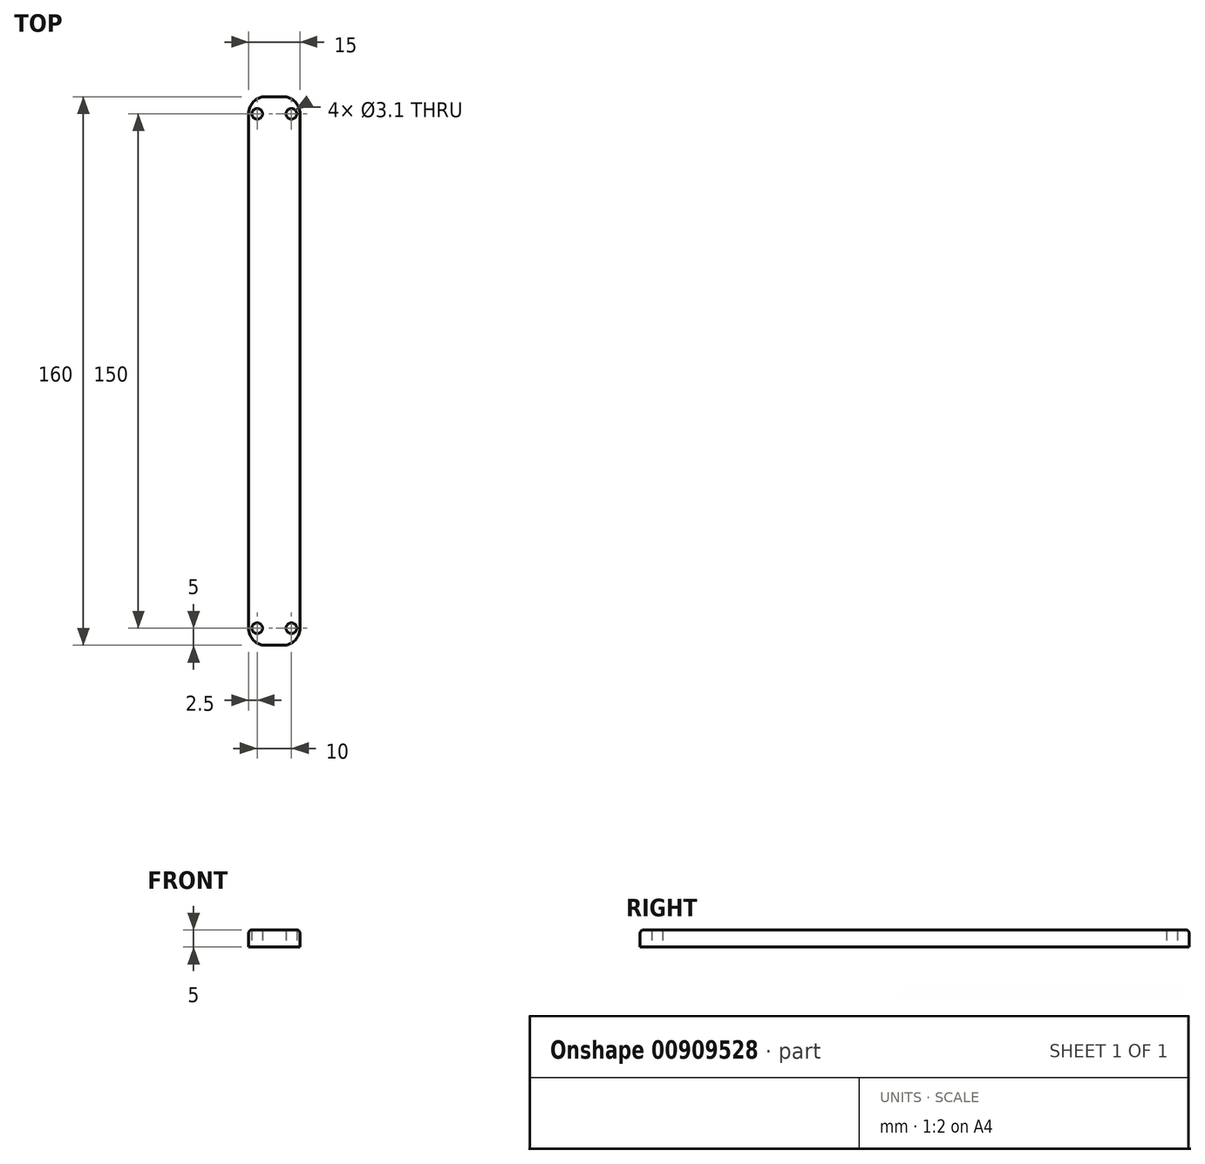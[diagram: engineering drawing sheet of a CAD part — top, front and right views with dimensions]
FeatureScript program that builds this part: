
annotation { "Feature Type Name" : "Feature", "Feature Type Description" : "" }
export const myFeature = defineFeature(function(context is Context, id is Id, definition is map)
    precondition{}
    {
        {
            var Q0;
            Q0=qCreatedBy(makeId("Top.planeOp"),FACE);
            var sketch = newSketch(context, id + "F0", { "sketchPlane" : qUnion([Q0])});
            skLineSegment(sketch, "E0.bottom", {"start": v(-7.5, -80) * mm, "end": v(7.5, -80) * mm});
            skLineSegment(sketch, "E0.top", {"start": v(-7.5, 80) * mm, "end": v(7.5, 80) * mm});
            skLineSegment(sketch, "E0.left", {"start": v(-7.5, -80) * mm, "end": v(-7.5, 80) * mm});
            skLineSegment(sketch, "E0.right", {"start": v(7.5, -80) * mm, "end": v(7.5, 80) * mm});
            skPoint(sketch, "E0.middle", {"position": v(0, 0) * mm});
            skLineSegment(sketch, "E1", {"start": v(0, 0) * mm, "end": v(0, 75) * mm});
            skLineSegment(sketch, "E2", {"start": v(0, 0) * mm, "end": v(0, -75) * mm});
            skLineSegment(sketch, "E3", {"start": v(0, -75) * mm, "end": v(-5, -75) * mm});
            skCircle(sketch, "E4", {"center": v(-5, -75) * mm, "radius": 1.55 * mm});
            skLineSegment(sketch, "E5", {"start": v(0, -75) * mm, "end": v(5, -75) * mm});
            skCircle(sketch, "E6", {"center": v(5, -75) * mm, "radius": 1.55 * mm});
            skLineSegment(sketch, "E7", {"start": v(0, 75) * mm, "end": v(5, 75) * mm});
            skLineSegment(sketch, "E8", {"start": v(0, 75) * mm, "end": v(-5, 75) * mm});
            skCircle(sketch, "E9", {"center": v(-5, 75) * mm, "radius": 1.55 * mm});
            skCircle(sketch, "E10", {"center": v(5, 75) * mm, "radius": 1.55 * mm});
            skSolve(sketch);
        }
        {
            var Q0;
            {var subQ6=sQuery(id+"F0.wireOp",EDGE,"E0.bottom");Q0=makeQuery(id+"F0.imprint","IMPRINT",FACE,{"disambiguationData":[TD([[makeQuery(id+"F0.imprint","IMPRINT",EDGE,{"derivedFrom":subQ6}),1.0]])]});}
            extrude(context, id + "F1", {"entities" : qUnion([Q0]), "depth" : 5 * mm, "offsetDistance" : 25 * mm});
        }
        {
            var Q0;
            Q0=makeQuery(id+"F1.opExtrude","SWEPT_EDGE",EDGE,{"disambiguationData":[OSD([sQuery(id+"F0.wireOp",EDGE,"E0.bottom"),sQuery(id+"F0.wireOp",EDGE,"E0.right")])]});
            var Q1;
            Q1=makeQuery(id+"F1.opExtrude","SWEPT_EDGE",EDGE,{"disambiguationData":[OSD([sQuery(id+"F0.wireOp",EDGE,"E0.bottom"),sQuery(id+"F0.wireOp",EDGE,"E0.left")])]});
            var Q2;
            Q2=makeQuery(id+"F1.opExtrude","SWEPT_EDGE",EDGE,{"disambiguationData":[OSD([sQuery(id+"F0.wireOp",EDGE,"E0.top"),sQuery(id+"F0.wireOp",EDGE,"E0.right")])]});
            var Q3;
            Q3=makeQuery(id+"F1.opExtrude","SWEPT_EDGE",EDGE,{"disambiguationData":[OSD([sQuery(id+"F0.wireOp",EDGE,"E0.top"),sQuery(id+"F0.wireOp",EDGE,"E0.left")])]});
            fillet(context, id + "F2", {"entities" : qUnion([Q0, Q1, Q2, Q3]), "radius" : 5 * mm, "tangentPropagation" : true, "allowEdgeOverflow" : false});
        }
        {
            var Q0;
            Q0=makeQuery(id+"F1.opExtrude","CAP_EDGE",EDGE,{"disambiguationData":[OSD([sQuery(id+"F0.wireOp",EDGE,"E0.right")])],"isStart":false});
            var Q1;
            Q1=makeQuery(id+"F1.opExtrude","CAP_EDGE",EDGE,{"disambiguationData":[OSD([sQuery(id+"F0.wireOp",EDGE,"E0.left")])],"isStart":false});
            fillet(context, id + "F3", {"entities" : qUnion([Q0, Q1]), "radius" : 1 * mm, "tangentPropagation" : true, "allowEdgeOverflow" : false});
        }
    });
